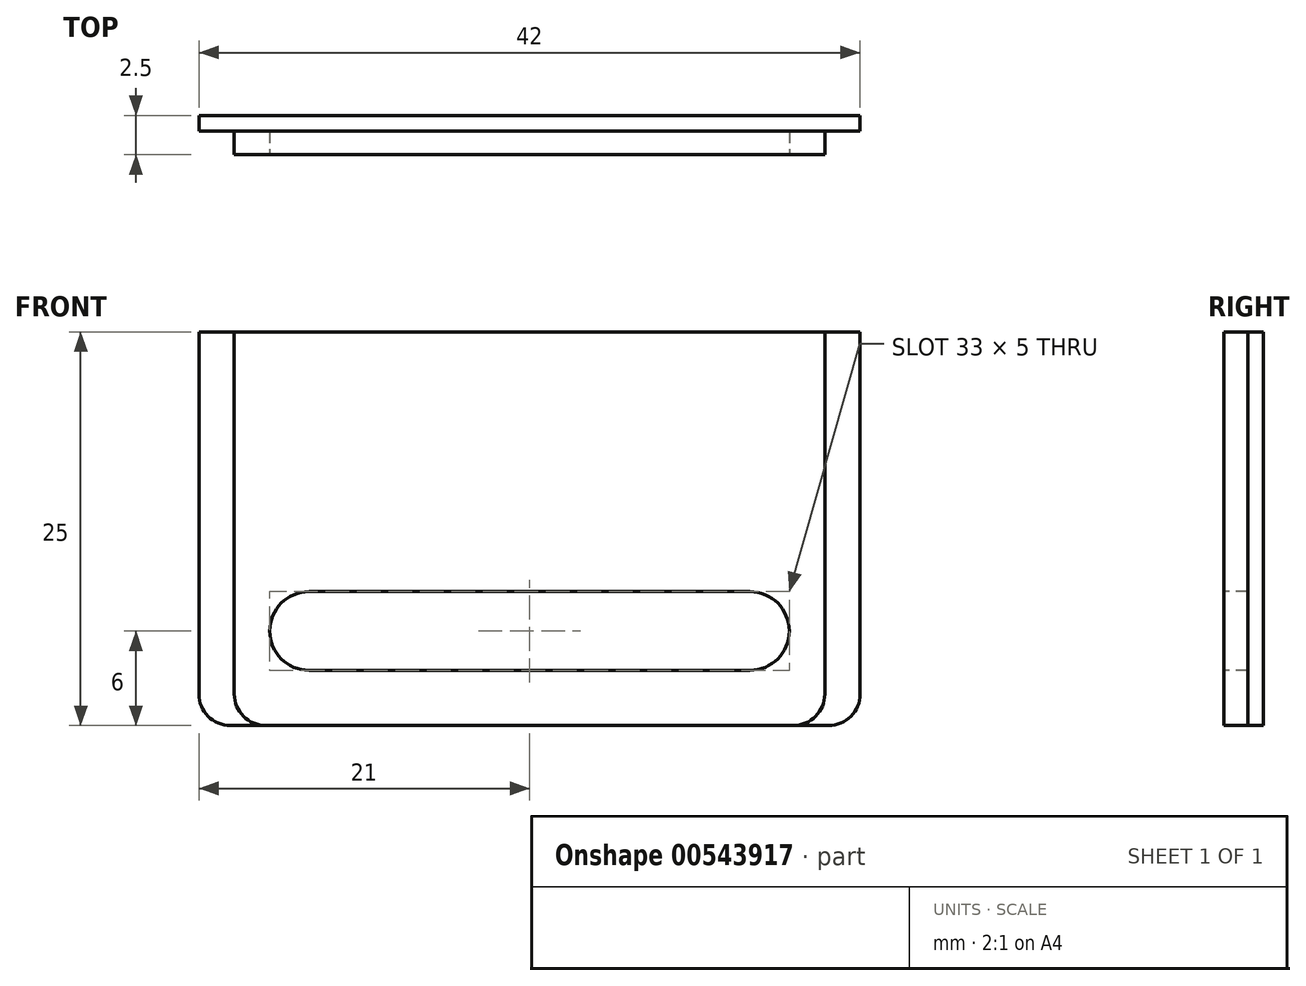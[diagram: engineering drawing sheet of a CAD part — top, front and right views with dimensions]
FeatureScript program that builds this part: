
annotation { "Feature Type Name" : "Feature", "Feature Type Description" : "" }
export const myFeature = defineFeature(function(context is Context, id is Id, definition is map)
    precondition{}
    {
        {
            var Q0;
            Q0=qCreatedBy(makeId("Front.planeOp"),FACE);
            var sketch = newSketch(context, id + "F0", { "sketchPlane" : qUnion([Q0])});
            skLineSegment(sketch, "E0.bottom", {"start": v(2, 0) * mm, "end": v(40, 0) * mm});
            skLineSegment(sketch, "E0.top", {"start": v(0, 25) * mm, "end": v(42, 25) * mm});
            skLineSegment(sketch, "E0.left", {"start": v(0, 2) * mm, "end": v(0, 25) * mm});
            skLineSegment(sketch, "E0.right", {"start": v(42, 2) * mm, "end": v(42, 25) * mm});
            skPoint(sketch, "E1.visualSharp", {"position": v(0, 0) * mm});
            skArc(sketch, "E1.filletArc", {"start": v(0, 2) * mm, "mid": v(0.59, 0.59) * mm, "end": v(2, 0) * mm});
            skPoint(sketch, "E2.visualSharp", {"position": v(42, 0) * mm});
            skArc(sketch, "E2.filletArc", {"start": v(40, 0) * mm, "mid": v(41.41, 0.59) * mm, "end": v(42, 2) * mm});
            skSolve(sketch);
        }
        {
            var Q0;
            Q0=qSketchRegion(id+"F0",true);
            extrude(context, id + "F1", {"entities" : qUnion([Q0]), "depth" : 1 * mm});
        }
        {
            var Q0;
            Q0=makeQuery(id+"F1.opExtrude","CAP_FACE",FACE,{"disambiguationData":[OSD([sQuery(id+"F0.wireOp",EDGE,"E0.bottom"),sQuery(id+"F0.wireOp",EDGE,"E0.top"),sQuery(id+"F0.wireOp",EDGE,"E0.left"),sQuery(id+"F0.wireOp",EDGE,"E0.right")])],"isStart":false});
            var sketch = newSketch(context, id + "F2", { "sketchPlane" : qUnion([Q0])});
            skLineSegment(sketch, "E3.bottom", {"start": v(2.25, 25) * mm, "end": v(39.75, 25) * mm});
            skLineSegment(sketch, "E3.top", {"start": v(4.25, 0) * mm, "end": v(37.75, 0) * mm});
            skLineSegment(sketch, "E3.left", {"start": v(2.25, 25) * mm, "end": v(2.25, 2) * mm});
            skLineSegment(sketch, "E3.right", {"start": v(39.75, 25) * mm, "end": v(39.75, 2) * mm});
            skPoint(sketch, "E4", {"position": v(21, 25) * mm});
            skPoint(sketch, "E5.visualSharp", {"position": v(2.25, 0) * mm});
            skArc(sketch, "E5.filletArc", {"start": v(2.25, 2) * mm, "mid": v(2.84, 0.59) * mm, "end": v(4.25, 0) * mm});
            skPoint(sketch, "E6.visualSharp", {"position": v(39.75, 0) * mm});
            skArc(sketch, "E6.filletArc", {"start": v(37.75, 0) * mm, "mid": v(39.16, 0.59) * mm, "end": v(39.75, 2) * mm});
            skSolve(sketch);
        }
        {
            var Q0;
            Q0=qSketchRegion(id+"F2",true);
            extrude(context, id + "F3", {"entities" : qUnion([Q0]), "depth" : 1.5 * mm});
        }
        {
            var Q0;
            Q0=makeQuery(id+"F3.opExtrude","CAP_FACE",FACE,{"disambiguationData":[OSD([sQuery(id+"F2.wireOp",EDGE,"E3.bottom"),sQuery(id+"F2.wireOp",EDGE,"E3.top"),sQuery(id+"F2.wireOp",EDGE,"E3.left"),sQuery(id+"F2.wireOp",EDGE,"E3.right"),sQuery(id+"F2.wireOp",EDGE,"E5.filletArc"),sQuery(id+"F2.wireOp",EDGE,"E6.filletArc")])],"isStart":false});
            var sketch = newSketch(context, id + "F4", { "sketchPlane" : qUnion([Q0])});
            skLineSegment(sketch, "E7", {"start": v(7, 8.5) * mm, "end": v(35, 8.5) * mm});
            skLineSegment(sketch, "E8", {"start": v(35, 3.5) * mm, "end": v(7, 3.5) * mm});
            skArc(sketch, "E9", {"start": v(7, 8.5) * mm, "mid": v(4.5, 6) * mm, "end": v(7, 3.5) * mm});
            skArc(sketch, "E10", {"start": v(35, 3.5) * mm, "mid": v(37.5, 6) * mm, "end": v(35, 8.5) * mm});
            skPoint(sketch, "E11", {"position": v(21, 0) * mm});
            skPoint(sketch, "E12", {"position": v(21, 3.5) * mm});
            skSolve(sketch);
        }
        {
            var Q0;
            Q0 = qSketchRegion(id + "F4", true);
            extrude(context, id + "F5", {"entities" : qUnion([Q0]), "operationType" : NewBodyOperationType.REMOVE, "endBound" : BoundingType.UP_TO_NEXT, "oppositeDirection" : true, "depth" : 25 * mm, "offsetDistance" : 25 * mm});
        }
    });
